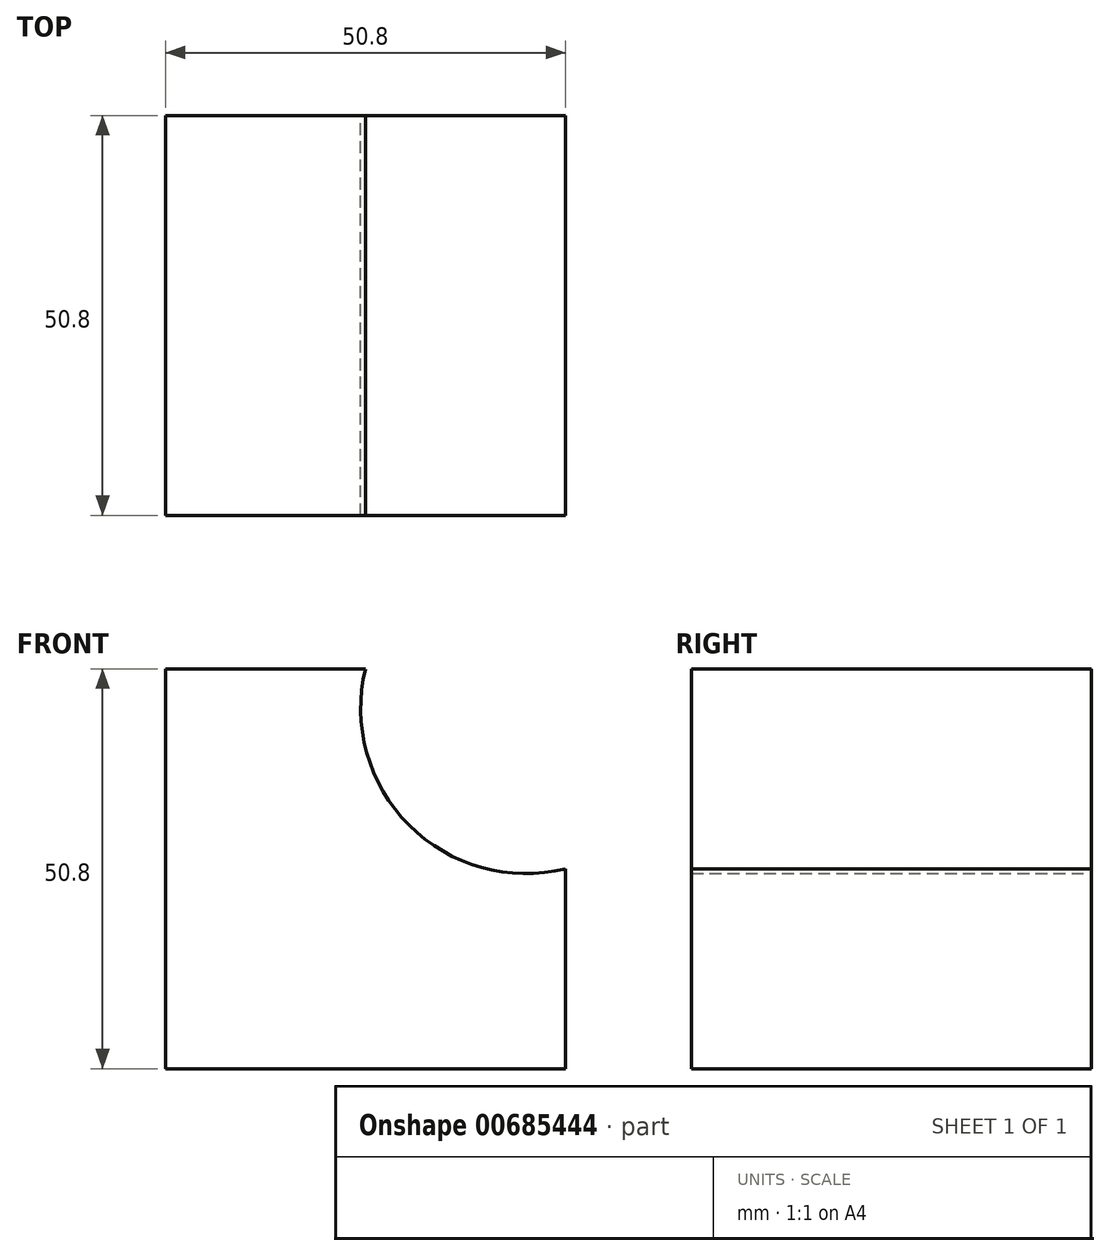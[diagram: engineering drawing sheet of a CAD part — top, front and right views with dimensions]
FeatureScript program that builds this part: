
annotation { "Feature Type Name" : "Feature", "Feature Type Description" : "" }
export const myFeature = defineFeature(function(context is Context, id is Id, definition is map)
    precondition{}
    {
        {
            var Q0;
            Q0=qCreatedBy(makeId("Front.planeOp"),FACE);
            var sketch = newSketch(context, id + "F0", { "sketchPlane" : qUnion([Q0])});
            skLineSegment(sketch, "E0", {"start": v(-59.3, 58.47) * mm, "end": v(-59.3, 7.67) * mm});
            skLineSegment(sketch, "E1", {"start": v(-59.3, 58.47) * mm, "end": v(-33.9, 58.47) * mm});
            skLineSegment(sketch, "E2", {"start": v(-59.3, 7.67) * mm, "end": v(-8.5, 7.67) * mm});
            skLineSegment(sketch, "E3", {"start": v(-8.5, 7.67) * mm, "end": v(-8.5, 33.07) * mm});
            skArc(sketch, "E4", {"start": v(-33.9, 58.47) * mm, "mid": v(-28.37, 38.6) * mm, "end": v(-8.5, 33.07) * mm});
            skSolve(sketch);
        }
        {
            var Q0;
            Q0=makeQuery(id+"F0.imprint","IMPRINT",FACE,{"disambiguationData":[TD([[makeQuery(id+"F0.imprint","IMPRINT",EDGE,{"derivedFrom":sQuery(id+"F0.wireOp",EDGE,"E0")}),1.0]])]});
            extrude(context, id + "F1", {"entities" : qUnion([Q0]), "depth" : 50.8 * mm, "offsetDistance" : 25.4 * mm});
        }
    });
